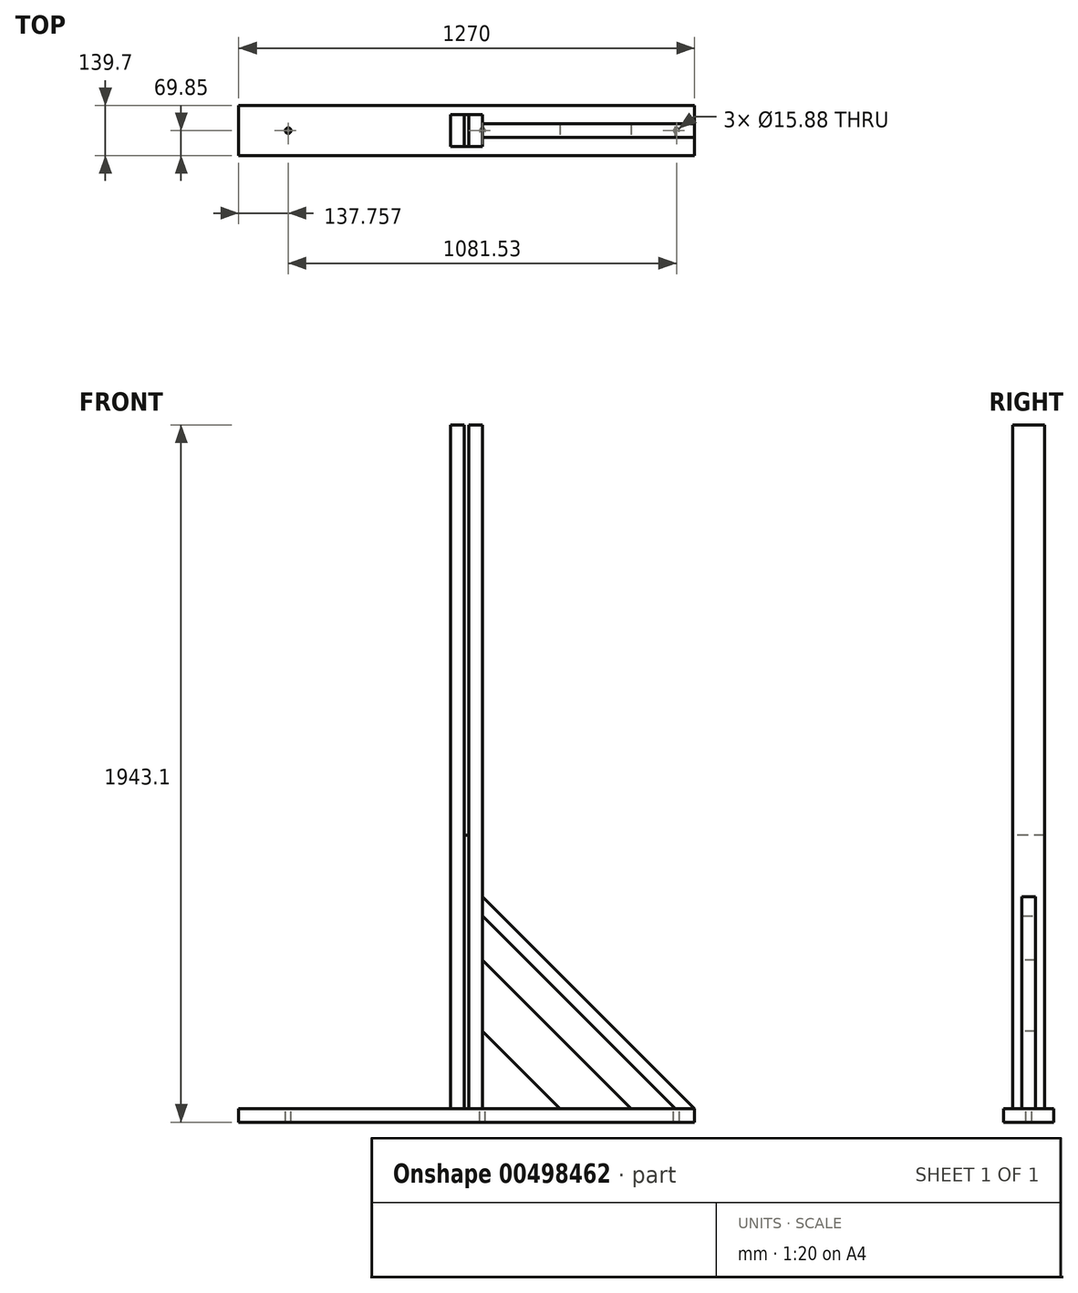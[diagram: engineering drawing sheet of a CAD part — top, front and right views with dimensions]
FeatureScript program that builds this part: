
annotation { "Feature Type Name" : "Feature", "Feature Type Description" : "" }
export const myFeature = defineFeature(function(context is Context, id is Id, definition is map)
    precondition{}
    {
        {
            var Q0;
            Q0=qCreatedBy(makeId("Top.planeOp"),FACE);
            var sketch = newSketch(context, id + "F0", { "sketchPlane" : qUnion([Q0])});
            skLineSegment(sketch, "E0.bottom", {"start": v(635, 69.85) * mm, "end": v(-635, 69.85) * mm});
            skLineSegment(sketch, "E0.top", {"start": v(635, -69.85) * mm, "end": v(-635, -69.85) * mm});
            skLineSegment(sketch, "E0.left", {"start": v(635, 69.85) * mm, "end": v(635, -69.85) * mm});
            skLineSegment(sketch, "E0.right", {"start": v(-635, 69.85) * mm, "end": v(-635, -69.85) * mm});
            skPoint(sketch, "E0.middle", {"position": v(0, 0) * mm});
            skSolve(sketch);
        }
        {
            var Q0;
            Q0=makeQuery(id+"F0.imprint","IMPRINT",FACE,{"disambiguationData":[TD([[makeQuery(id+"F0.imprint","IMPRINT",EDGE,{"derivedFrom":sQuery(id+"F0.wireOp",EDGE,"E0.bottom")}),1.0]])]});
            extrude(context, id + "F1", {"entities" : qUnion([Q0]), "depth" : 38.1 * mm});
        }
        {
            var Q0;
            Q0=makeQuery(id+"F1.opExtrude","CAP_FACE",FACE,{"disambiguationData":[OSD([sQuery(id+"F0.wireOp",EDGE,"E0.bottom"),sQuery(id+"F0.wireOp",EDGE,"E0.top"),sQuery(id+"F0.wireOp",EDGE,"E0.left"),sQuery(id+"F0.wireOp",EDGE,"E0.right")])],"isStart":false});
            var sketch = newSketch(context, id + "F2", { "sketchPlane" : qUnion([Q0])});
            skCircle(sketch, "E1.2.0.0", {"center": v(-497.24, 0) * mm, "radius": 7.94 * mm});
            skCircle(sketch, "E2.1.0.0", {"center": v(43.52, 0) * mm, "radius": 7.94 * mm});
            skLineSegment(sketch, "E2.direction1", {"start": v(-497.24, 0) * mm, "end": v(43.52, 0) * mm, "construction": true});
            skCircle(sketch, "E3.0.2.0", {"center": v(584.29, 0) * mm, "radius": 7.94 * mm});
            skSolve(sketch);
        }
        {
            var Q0;
            Q0 = qSketchRegion(id + "F2", true);
            var Q1;
            Q1=makeQuery(id+"F1.opExtrude","CAP_FACE",FACE,{"disambiguationData":[OSD([sQuery(id+"F0.wireOp",EDGE,"E0.bottom"),sQuery(id+"F0.wireOp",EDGE,"E0.top"),sQuery(id+"F0.wireOp",EDGE,"E0.left"),sQuery(id+"F0.wireOp",EDGE,"E0.right")])],"isStart":true});
            extrude(context, id + "F3", {"entities" : qUnion([Q0]), "operationType" : NewBodyOperationType.REMOVE, "endBound" : BoundingType.UP_TO_SURFACE, "oppositeDirection" : true, "endBoundEntityFace" : qUnion([Q1]), "depth" : 25.4 * mm});
        }
        {
            var Q0;
            Q0=makeQuery(id+"F1.opExtrude","CAP_FACE",FACE,{"disambiguationData":[OSD([sQuery(id+"F0.wireOp",EDGE,"E0.bottom"),sQuery(id+"F0.wireOp",EDGE,"E0.top"),sQuery(id+"F0.wireOp",EDGE,"E0.left"),sQuery(id+"F0.wireOp",EDGE,"E0.right")])],"isStart":false});
            var sketch = newSketch(context, id + "F4", { "sketchPlane" : qUnion([Q0])});
            skLineSegment(sketch, "E4.bottom", {"start": v(-6.35, 44.45) * mm, "end": v(6.35, 44.45) * mm});
            skLineSegment(sketch, "E4.top", {"start": v(-6.35, -44.45) * mm, "end": v(6.35, -44.45) * mm});
            skLineSegment(sketch, "E4.left", {"start": v(-6.35, 44.45) * mm, "end": v(-6.35, -44.45) * mm});
            skLineSegment(sketch, "E4.right", {"start": v(6.35, 44.45) * mm, "end": v(6.35, -44.45) * mm});
            skPoint(sketch, "E4.middle", {"position": v(0, 0) * mm});
            skSolve(sketch);
        }
        {
            var Q0;
            Q0 = qSketchRegion(id + "F4", true);
            extrude(context, id + "F5", {"entities" : qUnion([Q0]), "operationType" : NewBodyOperationType.ADD, "depth" : 762 * mm});
        }
        {
            var Q0;
            Q0=makeQuery(id+"F1.opExtrude","CAP_VERTEX",VERTEX,{"disambiguationData":[OSD([sQuery(id+"F0.wireOp",EDGE,"E0.bottom"),sQuery(id+"F0.wireOp",EDGE,"E0.right")])],"isStart":false});
            var Q1;
            Q1=makeQuery(id+"F1.opExtrude","CAP_VERTEX",VERTEX,{"disambiguationData":[OSD([sQuery(id+"F0.wireOp",EDGE,"E0.top"),sQuery(id+"F0.wireOp",EDGE,"E0.right")])],"isStart":false});
            var Q2;
            Q2=makeQuery(id+"F1.opExtrude","CAP_VERTEX",VERTEX,{"disambiguationData":[OSD([sQuery(id+"F0.wireOp",EDGE,"E0.top"),sQuery(id+"F0.wireOp",EDGE,"E0.left")])],"isStart":false});
            cPlane(context, id + "F6", {"entities" : qUnion([Q0, Q1, Q2]), "cplaneType" : CPlaneType.THREE_POINT, "offset" : 25.4 * mm, "width" : 152.4 * mm, "height" : 152.4 * mm});
        }
        {
            var Q0;
            Q0=qCreatedBy(id+"F6.planeOp",FACE);
            var sketch = newSketch(context, id + "F7", { "sketchPlane" : qUnion([Q0])});
            skLineSegment(sketch, "E5.bottom", {"start": v(6.35, -44.45) * mm, "end": v(44.45, -44.45) * mm});
            skLineSegment(sketch, "E5.top", {"start": v(6.35, 44.45) * mm, "end": v(44.45, 44.45) * mm});
            skLineSegment(sketch, "E5.left", {"start": v(6.35, -44.45) * mm, "end": v(6.35, 44.45) * mm});
            skLineSegment(sketch, "E5.right", {"start": v(44.45, -44.45) * mm, "end": v(44.45, 44.45) * mm});
            skLineSegment(sketch, "E6.bottom", {"start": v(-44.45, -44.45) * mm, "end": v(-6.35, -44.45) * mm});
            skLineSegment(sketch, "E6.top", {"start": v(-44.45, 44.45) * mm, "end": v(-6.35, 44.45) * mm});
            skLineSegment(sketch, "E6.left", {"start": v(-44.45, -44.45) * mm, "end": v(-44.45, 44.45) * mm});
            skLineSegment(sketch, "E6.right", {"start": v(-6.35, -44.45) * mm, "end": v(-6.35, 44.45) * mm});
            skLineSegment(sketch, "E7", {"start": v(-6.35, 0) * mm, "end": v(6.35, 0) * mm, "construction": true});
            skPoint(sketch, "E8", {"position": v(0, 0) * mm});
            skSolve(sketch);
        }
        {
            var Q0;
            Q0 = qSketchRegion(id + "F7", true);
            extrude(context, id + "F8", {"entities" : qUnion([Q0]), "oppositeDirection" : true, "depth" : 1905 * mm});
        }
        {
            var Q0;
            Q0=makeQuery(id+"F8.opExtrude","CAP_EDGE",EDGE,{"disambiguationData":[OSD([sQuery(id+"F7.wireOp",EDGE,"E5.right")])],"isStart":false});
            cPoint(context, id + "F9", {"entities" : qUnion([Q0]), "parameter" : 0.5});
        }
        {
            var Q0;
            Q0=makeQuery(id+"F8.opExtrude","CAP_EDGE",EDGE,{"disambiguationData":[OSD([sQuery(id+"F7.wireOp",EDGE,"E6.left")])],"isStart":false});
            cPoint(context, id + "F10", {"entities" : qUnion([Q0]), "parameter" : 0.5});
        }
        {
            var Q0;
            Q0=makeQuery(id+"F8.opExtrude","CAP_EDGE",EDGE,{"disambiguationData":[OSD([sQuery(id+"F7.wireOp",EDGE,"E5.right")])],"isStart":true});
            cPoint(context, id + "F11", {"entities" : qUnion([Q0]), "parameter" : 0.5});
        }
        {
            var Q0;
            Q0 = qCreatedBy(id + "F9" ,VERTEX);
            var Q1;
            Q1 = qCreatedBy(id + "F10" ,VERTEX);
            var Q2;
            Q2 = qCreatedBy(id + "F11" ,VERTEX);
            cPlane(context, id + "F12", {"entities" : qUnion([Q0, Q1, Q2]), "cplaneType" : CPlaneType.THREE_POINT, "offset" : 0 * mm, "width" : 152.4 * mm, "height" : 152.4 * mm});
        }
        {
            var Q0;
            Q0=qCreatedBy(id+"F12.planeOp",FACE);
            var sketch = newSketch(context, id + "F13", { "sketchPlane" : qUnion([Q0])});
            skLineSegment(sketch, "E9", {"start": v(-44.45, 574.77) * mm, "end": v(-581.12, 38.1) * mm});
            skLineSegment(sketch, "E10", {"start": v(-581.12, 38.1) * mm, "end": v(-44.45, 38.1) * mm, "construction": true});
            skLineSegment(sketch, "E11", {"start": v(-44.45, 38.1) * mm, "end": v(-44.45, 574.77) * mm, "construction": true});
            skLineSegment(sketch, "E12", {"start": v(-44.45, 628.65) * mm, "end": v(-635, 38.1) * mm});
            skLineSegment(sketch, "E13", {"start": v(-44.45, 574.77) * mm, "end": v(-44.45, 628.65) * mm});
            skLineSegment(sketch, "E14", {"start": v(-635, 38.1) * mm, "end": v(-581.12, 38.1) * mm});
            skSolve(sketch);
        }
        {
            var Q0;
            Q0 = qSketchRegion(id + "F13", true);
            extrude(context, id + "F14", {"entities" : qUnion([Q0]), "endBound" : BoundingType.SYMMETRIC, "oppositeDirection" : true, "depth" : 38.1 * mm, "hasSecondDirection" : true, "secondDirectionOppositeDirection" : true, "secondDirectionDepth" : 19.05 * mm});
        }
        {
            var Q0;
            Q0=qCreatedBy(id+"F12.planeOp",FACE);
            var sketch = newSketch(context, id + "F15", { "sketchPlane" : qUnion([Q0])});
            skLineSegment(sketch, "E15", {"start": v(-44.45, 451.2) * mm, "end": v(-457.54, 38.1) * mm});
            skLineSegment(sketch, "E16", {"start": v(-44.45, 253.63) * mm, "end": v(-259.98, 38.1) * mm});
            skLineSegment(sketch, "E17", {"start": v(-44.45, 451.2) * mm, "end": v(-44.45, 253.63) * mm});
            skLineSegment(sketch, "E18", {"start": v(-259.98, 38.1) * mm, "end": v(-457.54, 38.1) * mm});
            skSolve(sketch);
        }
        {
            var Q0;
            Q0 = qSketchRegion(id + "F15", true);
            extrude(context, id + "F16", {"entities" : qUnion([Q0]), "endBound" : BoundingType.SYMMETRIC, "depth" : 38.1 * mm});
        }
    });
